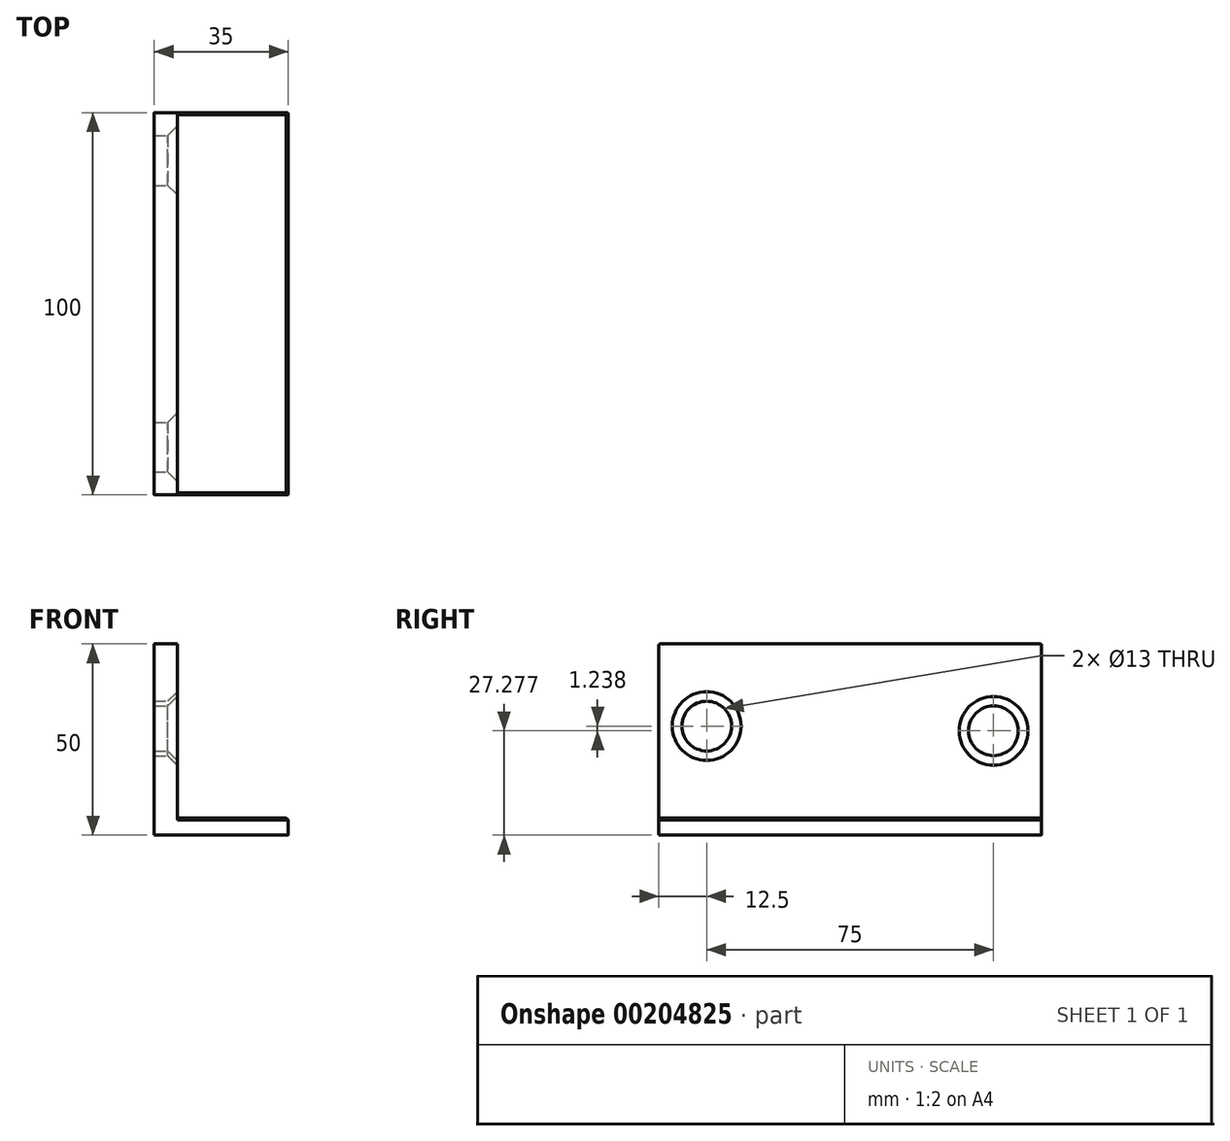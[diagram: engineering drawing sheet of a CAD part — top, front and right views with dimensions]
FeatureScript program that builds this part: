
annotation { "Feature Type Name" : "Feature", "Feature Type Description" : "" }
export const myFeature = defineFeature(function(context is Context, id is Id, definition is map)
    precondition{}
    {
        {
            var Q0;
            Q0=qCreatedBy(makeId("Front.planeOp"),FACE);
            var sketch = newSketch(context, id + "F0", { "sketchPlane" : qUnion([Q0])});
            skLineSegment(sketch, "E0", {"start": v(0, 0) * mm, "end": v(35, 0) * mm});
            skLineSegment(sketch, "E1", {"start": v(35, 0) * mm, "end": v(35, 4.5) * mm});
            skLineSegment(sketch, "E2", {"start": v(35, 4.5) * mm, "end": v(6, 4.5) * mm});
            skLineSegment(sketch, "E3", {"start": v(6, 4.5) * mm, "end": v(6, 50) * mm});
            skLineSegment(sketch, "E4", {"start": v(6, 50) * mm, "end": v(0, 50) * mm});
            skLineSegment(sketch, "E5", {"start": v(0, 50) * mm, "end": v(0, 0) * mm});
            skSolve(sketch);
        }
        {
            var Q0;
            Q0=makeQuery(id+"F0.imprint","IMPRINT",FACE,{"disambiguationData":[TD([[makeQuery(id+"F0.imprint","IMPRINT",EDGE,{"derivedFrom":sQuery(id+"F0.wireOp",EDGE,"E0")}),1.0]])]});
            extrude(context, id + "F1", {"entities" : qUnion([Q0]), "depth" : 100 * mm});
        }
        {
            var Q0;
            Q0=makeQuery(id+"F1.opExtrude","SWEPT_FACE",FACE,{"disambiguationData":[OSD([sQuery(id+"F0.wireOp",EDGE,"E3")])]});
            var sketch = newSketch(context, id + "F2", { "sketchPlane" : qUnion([Q0])});
            skCircle(sketch, "E6", {"center": v(-87.5, 28.51) * mm, "radius": 5 * mm});
            skCircle(sketch, "E7", {"center": v(-12.5, 27.28) * mm, "radius": 5 * mm});
            skSolve(sketch);
        }
        {
            var Q0;
            Q0=sQuery(id+"F2.wireOp",VERTEX,"E6.center");
            var Q1;
            Q1=sQuery(id+"F2.wireOp",VERTEX,"E7.center");
            var Q2;
            Q2=makeQuery(id+"F1.opExtrude","SWEPT_BODY",BODY,{"disambiguationData":[OSD([sQuery(id+"F0.wireOp",EDGE,"E0"),sQuery(id+"F0.wireOp",EDGE,"E1"),sQuery(id+"F0.wireOp",EDGE,"E2"),sQuery(id+"F0.wireOp",EDGE,"E3"),sQuery(id+"F0.wireOp",EDGE,"E4"),sQuery(id+"F0.wireOp",EDGE,"E5")])]});
            hole(context, id + "F3", {"style" : HoleStyle.C_SINK, "endStyle" : HoleEndStyle.BLIND, "holeDiameter" : 13 * mm, "cSinkDiameter" : 18 * mm, "cSinkAngle" : 90 * degree, "holeDepth" : 10 * mm, "startFromSketch" : true, "locations" : qUnion([Q0, Q1]), "scope" : qUnion([Q2])});
        }
        {
            var Q0;
            Q0=makeQuery(id+"F1.opExtrude","CAP_EDGE",EDGE,{"disambiguationData":[OSD([sQuery(id+"F0.wireOp",EDGE,"E2")])],"isStart":false});
            var Q1;
            Q1=makeQuery(id+"F1.opExtrude","SWEPT_EDGE",EDGE,{"disambiguationData":[OSD([sQuery(id+"F0.wireOp",EDGE,"E1"),sQuery(id+"F0.wireOp",EDGE,"E2")])]});
            var Q2;
            Q2=makeQuery(id+"F1.opExtrude","CAP_EDGE",EDGE,{"disambiguationData":[OSD([sQuery(id+"F0.wireOp",EDGE,"E2")])],"isStart":true});
            chamfer(context, id + "F4", {"entities" : qUnion([Q0, Q1, Q2]), "width" : .5 * mm, "tangentPropagation" : true});
        }
        {
            var Q0;
            Q0=makeQuery(id+"F1.opExtrude","CAP_EDGE",EDGE,{"disambiguationData":[OSD([sQuery(id+"F0.wireOp",EDGE,"E4")])],"isStart":false});
            var Q1;
            Q1=makeQuery(id+"F1.opExtrude","CAP_EDGE",EDGE,{"disambiguationData":[OSD([sQuery(id+"F0.wireOp",EDGE,"E4")])],"isStart":true});
            var Q2;
            Q2=makeQuery(id+"F1.opExtrude","CAP_EDGE",EDGE,{"disambiguationData":[OSD([sQuery(id+"F0.wireOp",EDGE,"E1")])],"isStart":false});
            var Q3;
            Q3=makeQuery(id+"F1.opExtrude","CAP_EDGE",EDGE,{"disambiguationData":[OSD([sQuery(id+"F0.wireOp",EDGE,"E1")])],"isStart":true});
            fillet(context, id + "F5", {"entities" : qUnion([Q0, Q1, Q2, Q3]), "radius" : .25 * mm, "tangentPropagation" : true, "allowEdgeOverflow" : false});
        }
    });
